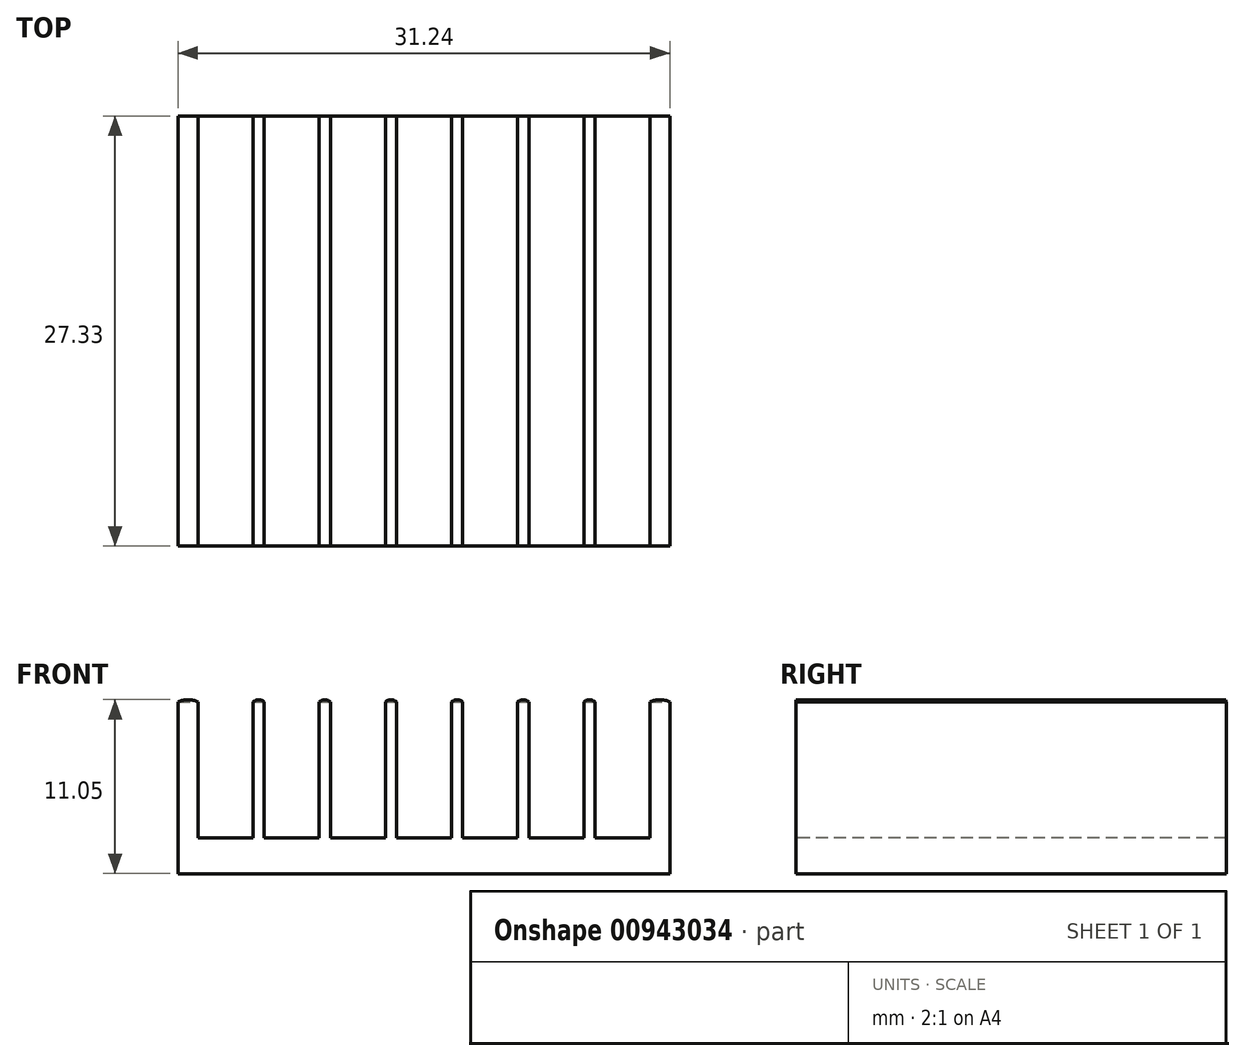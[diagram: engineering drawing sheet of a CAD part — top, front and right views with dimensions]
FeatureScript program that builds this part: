
annotation { "Feature Type Name" : "Feature", "Feature Type Description" : "" }
export const myFeature = defineFeature(function(context is Context, id is Id, definition is map)
    precondition{}
    {
        {
            var Q0;
            Q0=qCreatedBy(makeId("Front.planeOp"),FACE);
            var sketch = newSketch(context, id + "F0", { "sketchPlane" : qUnion([Q0])});
            skLineSegment(sketch, "E0", {"start": v(0, 0) * mm, "end": v(0, -8.64) * mm});
            skLineSegment(sketch, "E1", {"start": v(0, 0) * mm, "end": v(-1.27, 0) * mm});
            skLineSegment(sketch, "E2", {"start": v(-1.27, 0) * mm, "end": v(-1.27, -10.92) * mm});
            skLineSegment(sketch, "E3", {"start": v(-1.27, -10.92) * mm, "end": v(29.97, -10.92) * mm});
            skLineSegment(sketch, "E4", {"start": v(29.97, -10.92) * mm, "end": v(29.97, 0) * mm});
            skLineSegment(sketch, "E5", {"start": v(29.97, 0) * mm, "end": v(28.7, 0) * mm});
            skLineSegment(sketch, "E6", {"start": v(28.7, 0) * mm, "end": v(28.7, -8.64) * mm});
            skLineSegment(sketch, "E7", {"start": v(28.7, -8.64) * mm, "end": v(25.21, -8.64) * mm});
            skLineSegment(sketch, "E8", {"start": v(25.21, -8.64) * mm, "end": v(25.21, 0) * mm});
            skLineSegment(sketch, "E9", {"start": v(25.21, 0) * mm, "end": v(24.5, 0) * mm});
            skLineSegment(sketch, "E10", {"start": v(24.5, 0) * mm, "end": v(24.5, -8.64) * mm});
            skLineSegment(sketch, "E11", {"start": v(24.5, -8.64) * mm, "end": v(21.01, -8.64) * mm});
            skLineSegment(sketch, "E12", {"start": v(21.01, -8.64) * mm, "end": v(21.01, 0) * mm});
            skLineSegment(sketch, "E13", {"start": v(21.01, 0) * mm, "end": v(20.3, 0) * mm});
            skLineSegment(sketch, "E14", {"start": v(20.3, 0) * mm, "end": v(20.3, -8.64) * mm});
            skLineSegment(sketch, "E15", {"start": v(20.3, -8.64) * mm, "end": v(16.8, -8.64) * mm});
            skLineSegment(sketch, "E16", {"start": v(16.8, -8.64) * mm, "end": v(16.8, 0) * mm});
            skLineSegment(sketch, "E17", {"start": v(16.8, 0) * mm, "end": v(16.1, 0) * mm});
            skLineSegment(sketch, "E18", {"start": v(16.1, 0) * mm, "end": v(16.1, -8.64) * mm});
            skLineSegment(sketch, "E19", {"start": v(16.1, -8.64) * mm, "end": v(12.6, -8.64) * mm});
            skLineSegment(sketch, "E20", {"start": v(12.6, -8.64) * mm, "end": v(12.6, 0) * mm});
            skLineSegment(sketch, "E21", {"start": v(12.6, 0) * mm, "end": v(11.9, 0) * mm});
            skLineSegment(sketch, "E22", {"start": v(11.9, 0) * mm, "end": v(11.9, -8.64) * mm});
            skLineSegment(sketch, "E23", {"start": v(11.9, -8.64) * mm, "end": v(8.4, -8.64) * mm});
            skLineSegment(sketch, "E24", {"start": v(8.4, -8.64) * mm, "end": v(8.4, 0) * mm});
            skLineSegment(sketch, "E25", {"start": v(8.4, 0) * mm, "end": v(7.7, 0) * mm});
            skLineSegment(sketch, "E26", {"start": v(7.7, 0) * mm, "end": v(7.7, -8.64) * mm});
            skLineSegment(sketch, "E27", {"start": v(7.7, -8.64) * mm, "end": v(4.2, -8.64) * mm});
            skLineSegment(sketch, "E28", {"start": v(4.2, -8.64) * mm, "end": v(4.2, 0) * mm});
            skLineSegment(sketch, "E29", {"start": v(4.2, 0) * mm, "end": v(3.5, 0) * mm});
            skLineSegment(sketch, "E30", {"start": v(3.5, 0) * mm, "end": v(3.5, -8.64) * mm});
            skLineSegment(sketch, "E31", {"start": v(3.5, -8.64) * mm, "end": v(0, -8.64) * mm});
            skArc(sketch, "E32", {"start": v(0, 0) * mm, "mid": v(-0.64, 0.12) * mm, "end": v(-1.27, 0) * mm});
            skArc(sketch, "E33", {"start": v(4.2, 0) * mm, "mid": v(3.85, 0.13) * mm, "end": v(3.5, 0) * mm});
            skArc(sketch, "E34", {"start": v(8.4, 0) * mm, "mid": v(8.05, 0.13) * mm, "end": v(7.7, 0) * mm});
            skArc(sketch, "E35", {"start": v(12.6, 0) * mm, "mid": v(12.25, 0.13) * mm, "end": v(11.9, 0) * mm});
            skPoint(sketch, "E35.midSnap0", {"position": v(12.25, 0) * mm});
            skPoint(sketch, "E35.midSnap1", {"position": v(8.05, 0.13) * mm});
            skArc(sketch, "E36", {"start": v(16.8, 0) * mm, "mid": v(16.45, 0.13) * mm, "end": v(16.1, 0) * mm});
            skPoint(sketch, "E36.midSnap0", {"position": v(16.45, 0) * mm});
            skPoint(sketch, "E36.midSnap1", {"position": v(12.25, 0.13) * mm});
            skArc(sketch, "E37", {"start": v(21.01, 0) * mm, "mid": v(20.66, 0.13) * mm, "end": v(20.3, 0) * mm});
            skPoint(sketch, "E37.midSnap0", {"position": v(20.66, 0) * mm});
            skPoint(sketch, "E37.midSnap1", {"position": v(16.45, 0.13) * mm});
            skArc(sketch, "E38", {"start": v(25.21, 0) * mm, "mid": v(24.86, 0.13) * mm, "end": v(24.5, 0) * mm});
            skArc(sketch, "E39", {"start": v(29.97, 0) * mm, "mid": v(29.34, 0.13) * mm, "end": v(28.7, 0) * mm});
            skSolve(sketch);
        }
        {
            var Q0;
            Q0=makeQuery(id+"F0.imprint","IMPRINT",FACE,{"disambiguationData":[TD([[makeQuery(id+"F0.imprint","IMPRINT",EDGE,{"derivedFrom":sQuery(id+"F0.wireOp",EDGE,"E0")}),-1.0]])]});
            extrude(context, id + "F1", {"entities" : qUnion([Q0]), "oppositeDirection" : true, "depth" : 27.33 * mm, "offsetDistance" : 25.4 * mm});
        }
        {
            var Q0;
            Q0 = qSketchRegion(id + "F0", true);
            extrude(context, id + "F2", {"entities" : qUnion([Q0]), "operationType" : NewBodyOperationType.ADD, "oppositeDirection" : true, "depth" : 27.3 * mm, "offsetDistance" : 25.4 * mm});
        }
    });
